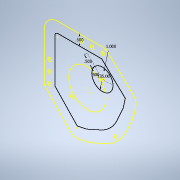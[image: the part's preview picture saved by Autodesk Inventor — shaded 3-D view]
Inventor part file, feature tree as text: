
AUTODESK INVENTOR PART (.ipt)
format: ipt  version: 2022 (Build 260153000, 153)  size: 104,960 bytes
history: native  units: in
note: dims shown in document units (in); Inventor stores cm internally (conversion verified against a paired STEP export)
features: other x3, sketch x1, reference x1
ambient origin geometry x8: Origin, YZ Plane, XZ Plane, XY Plane, X Axis, Y Axis, Z Axis, Center Point
feature tree (5):
  sketch  "Sketch1"  dims[d0=1.0in d1=0.5in d2=135.0deg d3=0.5in d4=0.5in]
  reference  "Reference1"
  other  "<userpath>\Documents\CAD\guardSwerve1\Assembly1.iam"
  other  "Assembly1.iam"
  other  "midblock"
